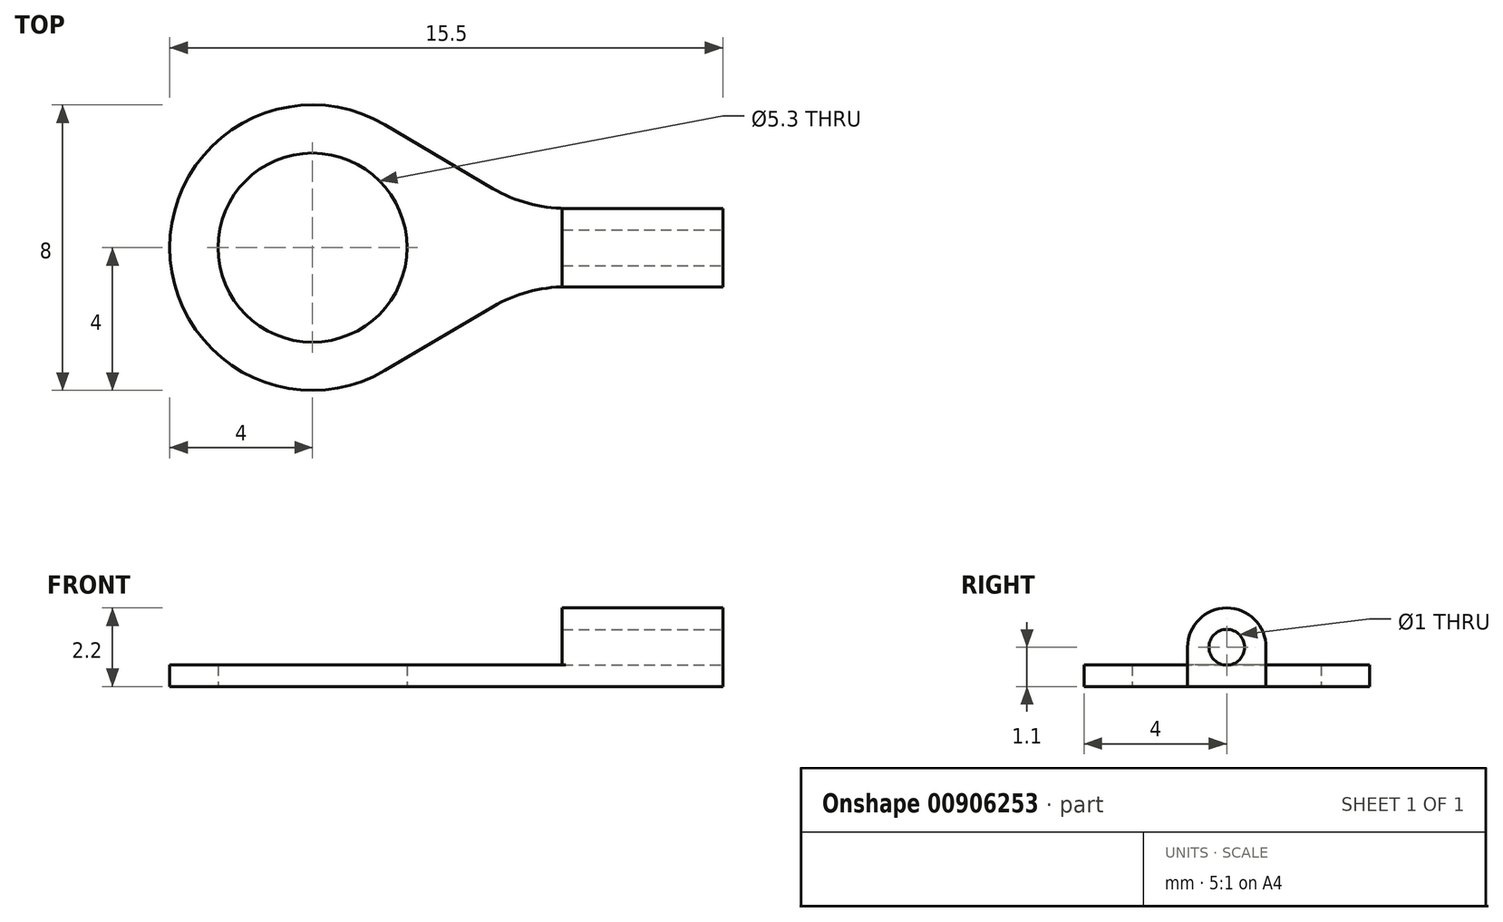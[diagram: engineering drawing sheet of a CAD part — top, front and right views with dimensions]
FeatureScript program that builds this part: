
annotation { "Feature Type Name" : "Feature", "Feature Type Description" : "" }
export const myFeature = defineFeature(function(context is Context, id is Id, definition is map)
    precondition{}
    {
        {
            var Q0;
            Q0=qCreatedBy(makeId("Top.planeOp"),FACE);
            var sketch = newSketch(context, id + "F0", { "sketchPlane" : qUnion([Q0])});
            skLineSegment(sketch, "E0", {"start": v(15.5, 2.9) * mm, "end": v(15.5, 5.1) * mm});
            skLineSegment(sketch, "E1", {"start": v(0, 4) * mm, "end": v(0, 4) * mm});
            skPoint(sketch, "E2.visualSharp", {"position": v(0, 8) * mm});
            skArc(sketch, "E2.filletArc", {"start": v(4, 8) * mm, "mid": v(1.17, 6.83) * mm, "end": v(0, 4) * mm});
            skPoint(sketch, "E3.visualSharp", {"position": v(0, 0) * mm});
            skArc(sketch, "E3.filletArc", {"start": v(0, 4) * mm, "mid": v(1.17, 1.17) * mm, "end": v(4, 0) * mm});
            skLineSegment(sketch, "E4.0", {"start": v(11, 2.9) * mm, "end": v(11, 5.1) * mm});
            skLineSegment(sketch, "E5.0", {"start": v(4, 0) * mm, "end": v(4, 8) * mm});
            skCircle(sketch, "E6", {"center": v(4, 4) * mm, "radius": 2.65 * mm});
            skLineSegment(sketch, "E7.0", {"start": v(15.5, 5.1) * mm, "end": v(11.1, 5.1) * mm});
            skLineSegment(sketch, "E8.0", {"start": v(15.5, 2.9) * mm, "end": v(11.1, 2.9) * mm});
            skArc(sketch, "E9", {"start": v(6.04, 7.44) * mm, "mid": v(0, 4) * mm, "end": v(6.04, 0.56) * mm});
            skLineSegment(sketch, "E10", {"start": v(9.06, 5.66) * mm, "end": v(6.04, 7.44) * mm});
            skLineSegment(sketch, "E11", {"start": v(9.06, 2.34) * mm, "end": v(6.04, 0.56) * mm});
            skPoint(sketch, "E12.orphan", {"position": v(15.5, 0) * mm});
            skPoint(sketch, "E13.end.orphan", {"position": v(10, 0) * mm});
            skPoint(sketch, "E14.orphan", {"position": v(15.5, 8) * mm});
            skPoint(sketch, "E15.orphan", {"position": v(10, 8) * mm});
            skPoint(sketch, "E16.visualSharp", {"position": v(10, 5.1) * mm});
            skArc(sketch, "E16.filletArc", {"start": v(9.06, 5.66) * mm, "mid": v(10.04, 5.24) * mm, "end": v(11.1, 5.1) * mm});
            skPoint(sketch, "E17.visualSharp", {"position": v(10, 2.9) * mm});
            skArc(sketch, "E17.filletArc", {"start": v(11.1, 2.9) * mm, "mid": v(10.04, 2.76) * mm, "end": v(9.06, 2.34) * mm});
            skPoint(sketch, "E18.orphan", {"position": v(10, 4) * mm});
            skPoint(sketch, "E19.start.orphan", {"position": v(15.5, 4) * mm});
            skSolve(sketch);
        }
        {
            var Q0;
            Q0 = qSketchRegion(id + "F0", true);
            extrude(context, id + "F1", {"entities" : qUnion([Q0]), "depth" : 0.6 * mm, "offsetDistance" : 25 * mm});
        }
        {
            var Q0;
            Q0=makeQuery(id+"F1.opExtrude","CAP_FACE",FACE,{"disambiguationData":[OSD([sQuery(id+"F0.wireOp",EDGE,"E0"),sQuery(id+"F0.wireOp",EDGE,"E6"),sQuery(id+"F0.wireOp",EDGE,"E7.0"),sQuery(id+"F0.wireOp",EDGE,"E8.0"),sQuery(id+"F0.wireOp",EDGE,"E9"),sQuery(id+"F0.wireOp",EDGE,"E10"),sQuery(id+"F0.wireOp",EDGE,"E11"),sQuery(id+"F0.wireOp",EDGE,"E16.filletArc"),sQuery(id+"F0.wireOp",EDGE,"E17.filletArc")])],"isStart":false});
            var sketch = newSketch(context, id + "F2", { "sketchPlane" : qUnion([Q0])});
            skLineSegment(sketch, "E20.bottom", {"start": v(15.5, 5.1) * mm, "end": v(11, 5.1) * mm});
            skLineSegment(sketch, "E20.top", {"start": v(15.5, 2.9) * mm, "end": v(11, 2.9) * mm});
            skLineSegment(sketch, "E20.left", {"start": v(15.5, 5.1) * mm, "end": v(15.5, 2.9) * mm});
            skLineSegment(sketch, "E20.right", {"start": v(11, 5.1) * mm, "end": v(11, 2.9) * mm});
            skSolve(sketch);
        }
        {
            var Q0;
            Q0 = qSketchRegion(id + "F2", true);
            extrude(context, id + "F3", {"entities" : qUnion([Q0]), "operationType" : NewBodyOperationType.ADD, "depth" : 1.6 * mm, "offsetDistance" : 25 * mm});
        }
        {
            var Q0;
            Q0=makeQuery(id+"F3.opExtrude","CAP_EDGE",EDGE,{"disambiguationData":[OSD([sQuery(id+"F2.wireOp",EDGE,"E20.bottom")])],"isStart":false});
            var Q1;
            Q1=makeQuery(id+"F3.opExtrude","CAP_EDGE",EDGE,{"disambiguationData":[OSD([sQuery(id+"F2.wireOp",EDGE,"E20.top")])],"isStart":false});
            fillet(context, id + "F4", {"entities" : qUnion([Q0, Q1]), "radius" : 1.1 * mm, "tangentPropagation" : true, "allowEdgeOverflow" : false});
        }
        {
            var Q0;
            Q0=makeQuery(id+"F3.boolean.opBoolean","MERGE",FACE,{"derivedFrom":[makeQuery(id+"F1.opExtrude","SWEPT_FACE",FACE,{"disambiguationData":[OSD([sQuery(id+"F0.wireOp",EDGE,"E0")])]}),makeQuery(id+"F3.opExtrude","SWEPT_FACE",FACE,{"disambiguationData":[OSD([sQuery(id+"F2.wireOp",EDGE,"E20.left")])]})]});
            var sketch = newSketch(context, id + "F5", { "sketchPlane" : qUnion([Q0])});
            skCircle(sketch, "E21", {"center": v(4, 1.1) * mm, "radius": 0.5 * mm});
            skSolve(sketch);
        }
        {
            var Q0;
            Q0 = qSketchRegion(id + "F5", true);
            extrude(context, id + "F6", {"entities" : qUnion([Q0]), "operationType" : NewBodyOperationType.REMOVE, "oppositeDirection" : true, "depth" : 25 * mm, "offsetDistance" : 25 * mm});
        }
    });
